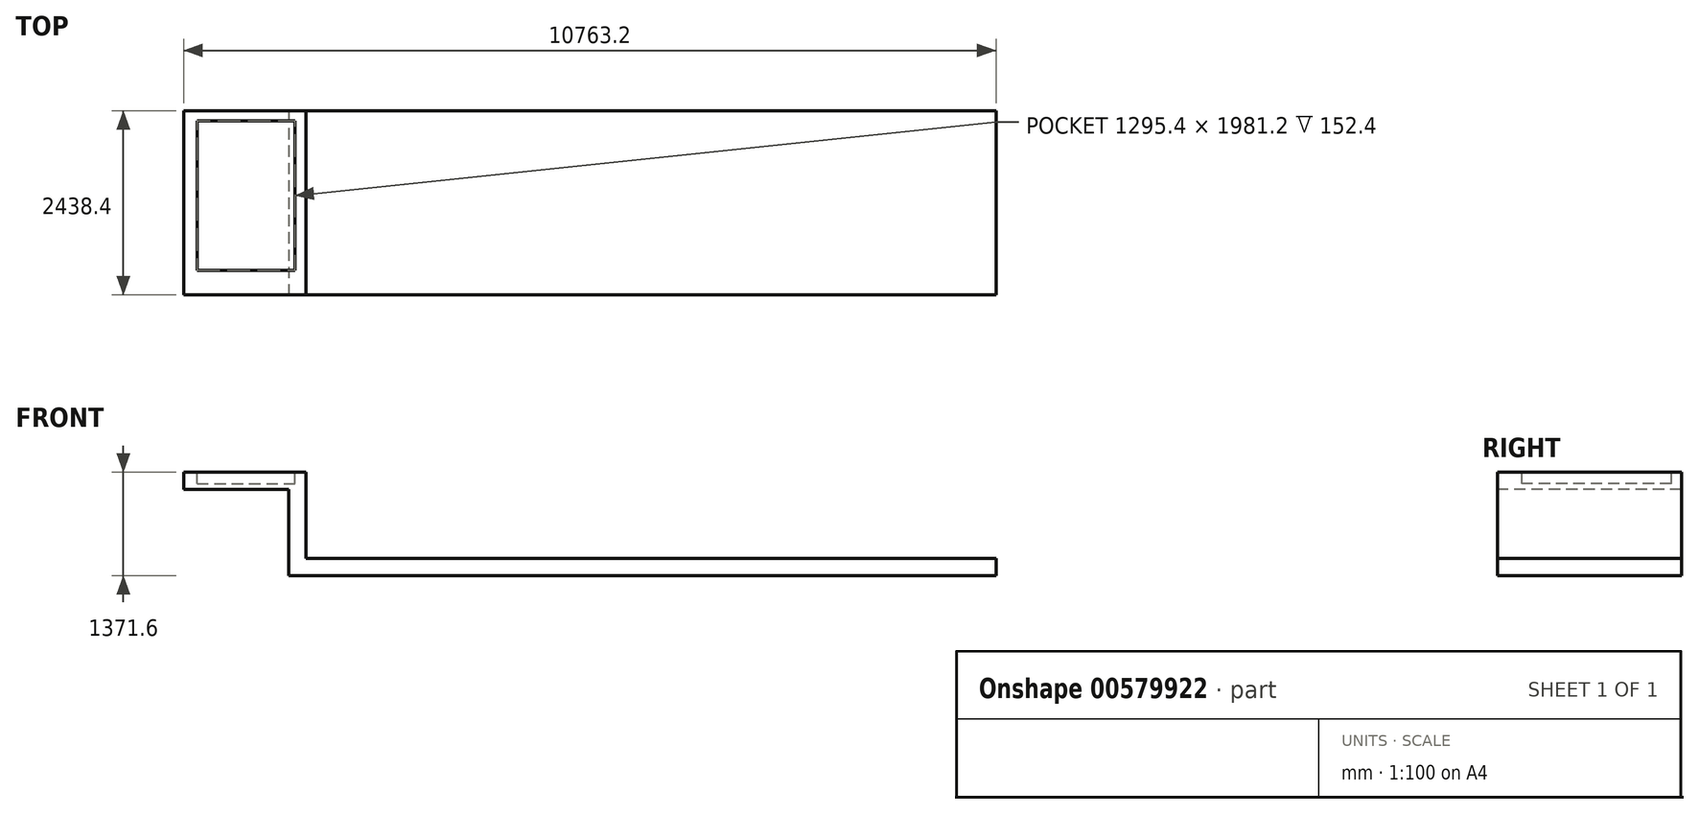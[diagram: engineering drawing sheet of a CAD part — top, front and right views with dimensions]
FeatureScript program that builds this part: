
annotation { "Feature Type Name" : "Feature", "Feature Type Description" : "" }
export const myFeature = defineFeature(function(context is Context, id is Id, definition is map)
    precondition{}
    {
        {
            var Q0;
            Q0=qCreatedBy(makeId("Top.planeOp"),FACE);
            var sketch = newSketch(context, id + "F0", { "sketchPlane" : qUnion([Q0])});
            skLineSegment(sketch, "E0.bottom", {"start": v(-5780.69, 2438.4) * mm, "end": v(3591.91, 2438.4) * mm});
            skLineSegment(sketch, "E0.top", {"start": v(-5780.69, 0) * mm, "end": v(3591.91, 0) * mm});
            skLineSegment(sketch, "E0.left", {"start": v(-5780.69, 2438.4) * mm, "end": v(-5780.69, 0) * mm});
            skLineSegment(sketch, "E0.right", {"start": v(3591.91, 2438.4) * mm, "end": v(3591.91, 0) * mm});
            skSolve(sketch);
        }
        {
            var Q0;
            Q0=makeQuery(id+"F0.imprint","IMPRINT",FACE,{"disambiguationData":[TD([[makeQuery(id+"F0.imprint","IMPRINT",EDGE,{"derivedFrom":sQuery(id+"F0.wireOp",EDGE,"E0.bottom")}),-1.0]])]});
            extrude(context, id + "F1", {"entities" : qUnion([Q0]), "depth" : 228.6 * mm, "offsetDistance" : 25.4 * mm});
        }
        {
            var Q0;
            Q0=makeQuery(id+"F1.opExtrude","CAP_FACE",FACE,{"disambiguationData":[OSD([sQuery(id+"F0.wireOp",EDGE,"E0.bottom"),sQuery(id+"F0.wireOp",EDGE,"E0.top"),sQuery(id+"F0.wireOp",EDGE,"E0.left"),sQuery(id+"F0.wireOp",EDGE,"E0.right")])],"isStart":false});
            var sketch = newSketch(context, id + "F2", { "sketchPlane" : qUnion([Q0])});
            skLineSegment(sketch, "E1.bottom", {"start": v(-5780.69, 2438.4) * mm, "end": v(-5552.09, 2438.4) * mm});
            skLineSegment(sketch, "E1.top", {"start": v(-5780.69, 0) * mm, "end": v(-5552.09, 0) * mm});
            skLineSegment(sketch, "E1.left", {"start": v(-5780.69, 2438.4) * mm, "end": v(-5780.69, 0) * mm});
            skLineSegment(sketch, "E1.right", {"start": v(-5552.09, 2438.4) * mm, "end": v(-5552.09, 0) * mm});
            skSolve(sketch);
        }
        {
            var Q0;
            Q0=makeQuery(id+"F2.imprint","IMPRINT",FACE,{"disambiguationData":[TD([[makeQuery(id+"F2.imprint","IMPRINT",EDGE,{"derivedFrom":sQuery(id+"F2.wireOp",EDGE,"E1.bottom")}),-1.0]])]});
            extrude(context, id + "F3", {"entities" : qUnion([Q0]), "operationType" : NewBodyOperationType.ADD, "depth" : 1143 * mm, "offsetDistance" : 25.4 * mm});
        }
        {
            var Q0;
            Q0=makeQuery(id+"F3.boolean.opBoolean","MERGE",FACE,{"derivedFrom":[makeQuery(id+"F1.opExtrude","SWEPT_FACE",FACE,{"disambiguationData":[OSD([sQuery(id+"F0.wireOp",EDGE,"E0.left")])]}),makeQuery(id+"F3.opExtrude","SWEPT_FACE",FACE,{"disambiguationData":[OSD([sQuery(id+"F2.wireOp",EDGE,"E1.left")])]})]});
            var sketch = newSketch(context, id + "F4", { "sketchPlane" : qUnion([Q0])});
            skLineSegment(sketch, "E2.bottom", {"start": v(-2438.4, 1371.6) * mm, "end": v(0, 1371.6) * mm});
            skLineSegment(sketch, "E2.top", {"start": v(-2438.4, 1143) * mm, "end": v(0, 1143) * mm});
            skLineSegment(sketch, "E2.left", {"start": v(-2438.4, 1371.6) * mm, "end": v(-2438.4, 1143) * mm});
            skLineSegment(sketch, "E2.right", {"start": v(0, 1371.6) * mm, "end": v(0, 1143) * mm});
            skSolve(sketch);
        }
        {
            var Q0;
            Q0=makeQuery(id+"F4.imprint","IMPRINT",FACE,{"disambiguationData":[TD([[makeQuery(id+"F4.imprint","IMPRINT",EDGE,{"derivedFrom":sQuery(id+"F4.wireOp",EDGE,"E2.bottom")}),-1.0]])]});
            extrude(context, id + "F5", {"entities" : qUnion([Q0]), "operationType" : NewBodyOperationType.ADD, "depth" : 1390.65 * mm, "offsetDistance" : 25.4 * mm});
        }
        {
            var Q0;
            Q0=makeQuery(id+"F5.boolean.opBoolean","MERGE",FACE,{"derivedFrom":[makeQuery(id+"F3.opExtrude","CAP_FACE",FACE,{"disambiguationData":[OSD([sQuery(id+"F2.wireOp",EDGE,"E1.bottom"),sQuery(id+"F2.wireOp",EDGE,"E1.top"),sQuery(id+"F2.wireOp",EDGE,"E1.left"),sQuery(id+"F2.wireOp",EDGE,"E1.right")])],"isStart":false}),makeQuery(id+"F5.opExtrude","SWEPT_FACE",FACE,{"disambiguationData":[OSD([sQuery(id+"F4.wireOp",EDGE,"E2.bottom")])]})]});
            var sketch = newSketch(context, id + "F6", { "sketchPlane" : qUnion([Q0])});
            skLineSegment(sketch, "E3.bottom", {"start": v(-6993.54, 2305.05) * mm, "end": v(-5698.14, 2305.05) * mm});
            skLineSegment(sketch, "E3.top", {"start": v(-6993.54, 323.85) * mm, "end": v(-5698.14, 323.85) * mm});
            skLineSegment(sketch, "E3.left", {"start": v(-6993.54, 2305.05) * mm, "end": v(-6993.54, 323.85) * mm});
            skLineSegment(sketch, "E3.right", {"start": v(-5698.14, 2305.05) * mm, "end": v(-5698.14, 323.85) * mm});
            skSolve(sketch);
        }
        {
            var Q0;
            Q0=makeQuery(id+"F6.imprint","IMPRINT",FACE,{"disambiguationData":[TD([[makeQuery(id+"F6.imprint","IMPRINT",EDGE,{"derivedFrom":sQuery(id+"F6.wireOp",EDGE,"E3.bottom")}),-1.0]])]});
            extrude(context, id + "F7", {"entities" : qUnion([Q0]), "operationType" : NewBodyOperationType.REMOVE, "oppositeDirection" : true, "depth" : 152.4 * mm, "offsetDistance" : 25.4 * mm});
        }
    });
